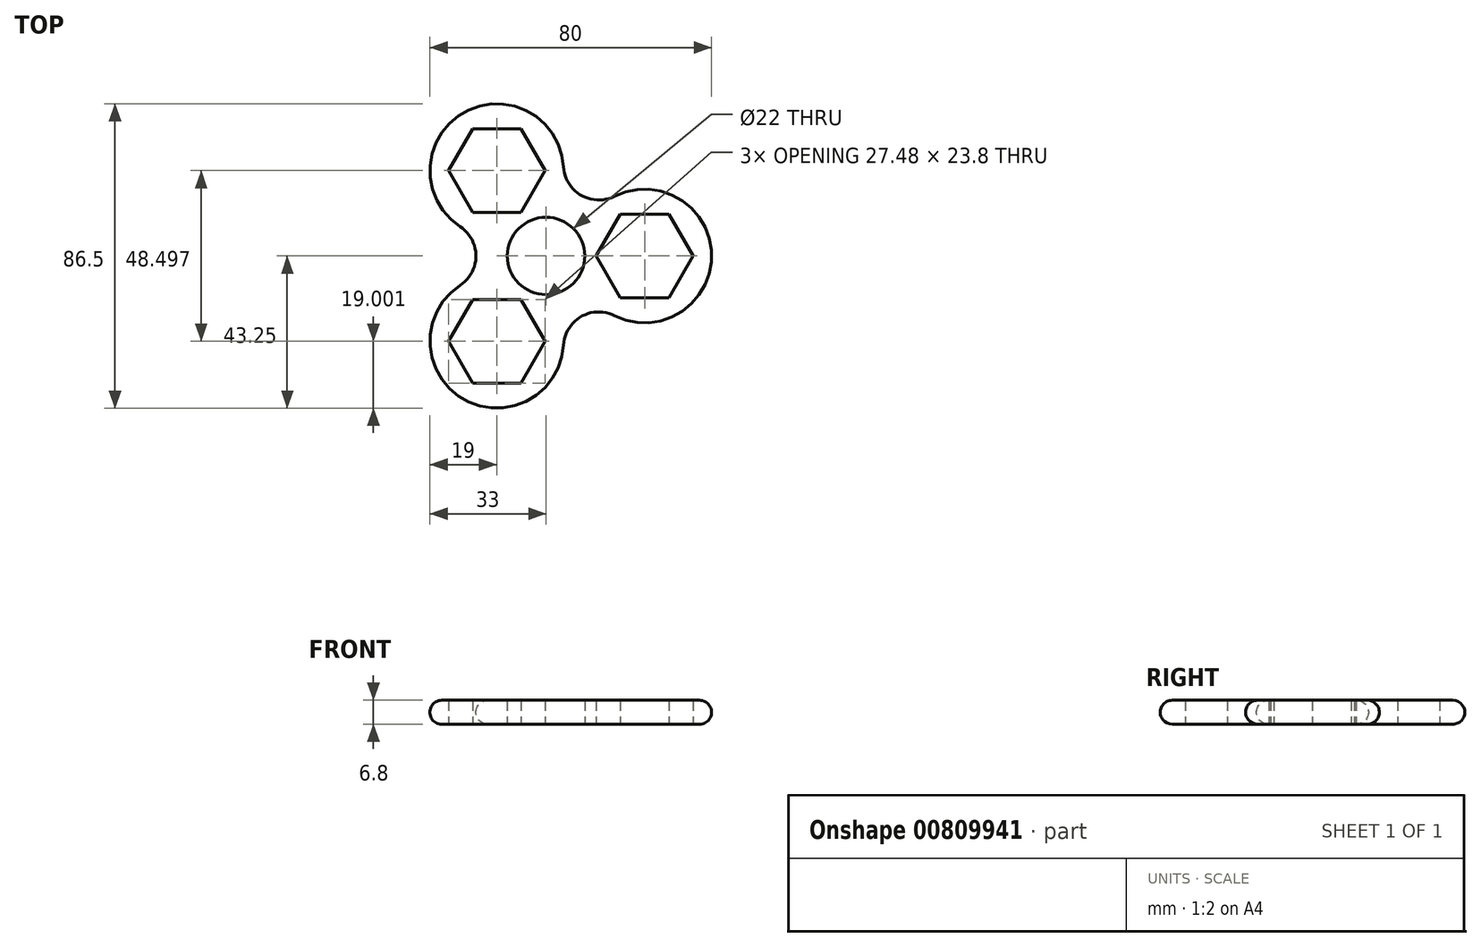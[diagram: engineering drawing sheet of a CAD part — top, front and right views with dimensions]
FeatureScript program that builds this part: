
annotation { "Feature Type Name" : "Feature", "Feature Type Description" : "" }
export const myFeature = defineFeature(function(context is Context, id is Id, definition is map)
    precondition{}
    {
        {
            var Q0;
            Q0=qCreatedBy(makeId("Top.planeOp"),FACE);
            var sketch = newSketch(context, id + "F0", { "sketchPlane" : qUnion([Q0])});
            skLineSegment(sketch, "E0", {"start": v(0, 0) * mm, "end": v(28, 0) * mm, "construction": true});
            skArc(sketch, "E1", {"start": v(19.45, -16.97) * mm, "mid": v(47, 0) * mm, "end": v(19.45, 16.97) * mm});
            skArc(sketch, "E2.1.1", {"start": v(4.97, 25.33) * mm, "mid": v(-23.5, 40.7) * mm, "end": v(-24.42, 8.36) * mm});
            skLineSegment(sketch, "E2.1.2", {"start": v(0, 0) * mm, "end": v(-14, 24.25) * mm, "construction": true});
            skArc(sketch, "E2.2.1", {"start": v(-24.42, -8.36) * mm, "mid": v(-23.5, -40.7) * mm, "end": v(4.97, -25.33) * mm});
            skLineSegment(sketch, "E2.2.2", {"start": v(0, 0) * mm, "end": v(-14, -24.25) * mm, "construction": true});
            skArc(sketch, "E3", {"start": v(4.97, 25.33) * mm, "mid": v(9.95, 17.24) * mm, "end": v(19.45, 16.97) * mm});
            skArc(sketch, "E4.1.0", {"start": v(-24.42, -8.36) * mm, "mid": v(-19.9, 0) * mm, "end": v(-24.42, 8.36) * mm});
            skArc(sketch, "E4.2.0", {"start": v(19.45, -16.97) * mm, "mid": v(9.95, -17.24) * mm, "end": v(4.97, -25.33) * mm});
            skPoint(sketch, "E4.center", {"position": v(0, 0) * mm});
            skCircle(sketch, "E5", {"center": v(0, 0) * mm, "radius": 11 * mm});
            skCircle(sketch, "E6.cCircle", {"center": v(-14, -24.25) * mm, "radius": 11.9 * mm, "construction": true});
            skLineSegment(sketch, "E6.0", {"start": v(-7.13, -12.35) * mm, "end": v(-0.26, -24.25) * mm});
            skLineSegment(sketch, "E6.1", {"start": v(-0.26, -24.25) * mm, "end": v(-7.13, -36.15) * mm});
            skLineSegment(sketch, "E6.2", {"start": v(-7.13, -36.15) * mm, "end": v(-20.87, -36.15) * mm});
            skLineSegment(sketch, "E6.3", {"start": v(-20.87, -36.15) * mm, "end": v(-27.74, -24.25) * mm});
            skLineSegment(sketch, "E6.4", {"start": v(-27.74, -24.25) * mm, "end": v(-20.87, -12.35) * mm});
            skLineSegment(sketch, "E6.5", {"start": v(-20.87, -12.35) * mm, "end": v(-7.13, -12.35) * mm});
            skPoint(sketch, "E6.0.midPoint", {"position": v(-3.7, -18.3) * mm});
            skLineSegment(sketch, "E7.1.0", {"start": v(41.74, 0) * mm, "end": v(34.87, -11.9) * mm});
            skPoint(sketch, "E7.1.1", {"position": v(17.7, 5.95) * mm});
            skLineSegment(sketch, "E7.1.2", {"start": v(34.87, -11.9) * mm, "end": v(21.13, -11.9) * mm});
            skCircle(sketch, "E7.1.3", {"center": v(28, 0) * mm, "radius": 11.9 * mm, "construction": true});
            skLineSegment(sketch, "E7.1.4", {"start": v(34.87, 11.9) * mm, "end": v(41.74, 0) * mm});
            skLineSegment(sketch, "E7.1.5", {"start": v(21.13, -11.9) * mm, "end": v(14.26, 0) * mm});
            skLineSegment(sketch, "E7.1.6", {"start": v(14.26, 0) * mm, "end": v(21.13, 11.9) * mm});
            skLineSegment(sketch, "E7.1.7", {"start": v(21.13, 11.9) * mm, "end": v(34.87, 11.9) * mm});
            skLineSegment(sketch, "E7.2.0", {"start": v(-20.87, 36.15) * mm, "end": v(-7.13, 36.15) * mm});
            skPoint(sketch, "E7.2.1", {"position": v(-14, 12.35) * mm});
            skLineSegment(sketch, "E7.2.2", {"start": v(-7.13, 36.15) * mm, "end": v(-0.26, 24.25) * mm});
            skCircle(sketch, "E7.2.3", {"center": v(-14, 24.25) * mm, "radius": 11.9 * mm, "construction": true});
            skLineSegment(sketch, "E7.2.4", {"start": v(-27.74, 24.25) * mm, "end": v(-20.87, 36.15) * mm});
            skLineSegment(sketch, "E7.2.5", {"start": v(-0.26, 24.25) * mm, "end": v(-7.13, 12.35) * mm});
            skLineSegment(sketch, "E7.2.6", {"start": v(-7.13, 12.35) * mm, "end": v(-20.87, 12.35) * mm});
            skLineSegment(sketch, "E7.2.7", {"start": v(-20.87, 12.35) * mm, "end": v(-27.74, 24.25) * mm});
            skSolve(sketch);
        }
        {
            var Q0;
            Q0 = qSketchRegion(id + "F0", true);
            extrude(context, id + "F1", {"entities" : qUnion([Q0]), "depth" : 6.8 * mm, "offsetDistance" : 25 * mm});
        }
        {
            var Q0;
            Q0=makeQuery(id+"F1.opExtrude","CAP_EDGE",EDGE,{"disambiguationData":[OSD([sQuery(id+"F0.wireOp",EDGE,"E2.1.1")])],"isStart":false});
            var Q1;
            Q1=makeQuery(id+"F1.opExtrude","CAP_EDGE",EDGE,{"disambiguationData":[OSD([sQuery(id+"F0.wireOp",EDGE,"E3")])],"isStart":true});
            fillet(context, id + "F2", {"entities" : qUnion([Q0, Q1]), "radius" : 3.4 * mm, "tangentPropagation" : true, "allowEdgeOverflow" : false});
        }
    });
